# Revit family: O5MH-NRG-
name_source: partatom
category: Mechanical Equipment
revit_build: Autodesk Revit 2015 (Build: 20140606_1530(x64)
units: mm (PartAtom-declared; Revit-internal decimal feet)

## types (4) — shared parameters
20" Shelf = Yes
BOTTOM ELECTRICAL = Yes
BOTTOM REFRIGERATION PIPING = Yes
Certifications = NSF 7, UL471, CSA
DATE = DOE 2017
DRAIN PIPING = Yes
Description = High Multi-Deck Merchandiser
EQUIPMENT DESCRIPTION = High Multi-Deck Merchandiser
EQUIPMENT MARK = O5MH-NRG
GLASS = Glass
Height = 85 5/8"
Item Description = High Multi-Deck Merchandiser
LF STD END = Yes
Legend Number = O5MH-NRG
Manufacturer = HILLPHOENIX
Model = O5MH-NRG
PAINTED METAL UPPER SHELF = PAINTED SHELVES
REAR REFRIGERATION PIPING = Yes
REFRIGERATION PIPING = COPPER PIPE
RT STD END = Yes
STAINLESS STEEL = GALVANIZED STEEL
TOP ELECTRICAL = Yes
TOP REFRIGERATION PIPING = Yes
URL = http://www.hillphoenix.com
Width = 43 1/8"

## per-type parameters (varying)
| type | CENTER LINE | DRAIN LINE | Length | Refgn |
| 4' | 24" | 36" | 48" | 22 1/2" |
| 6' | 36" | 36" | 72" | 28 5/8" |
| 8' | 48" | 48" | 96" | 28 5/8" |
| 12' | 72" | 72" | 144" | 28 5/8" |

## geometry (parser evidence)
native form markers: Blend x10, Sweep x3
no freeform markers — native parametric forms only
